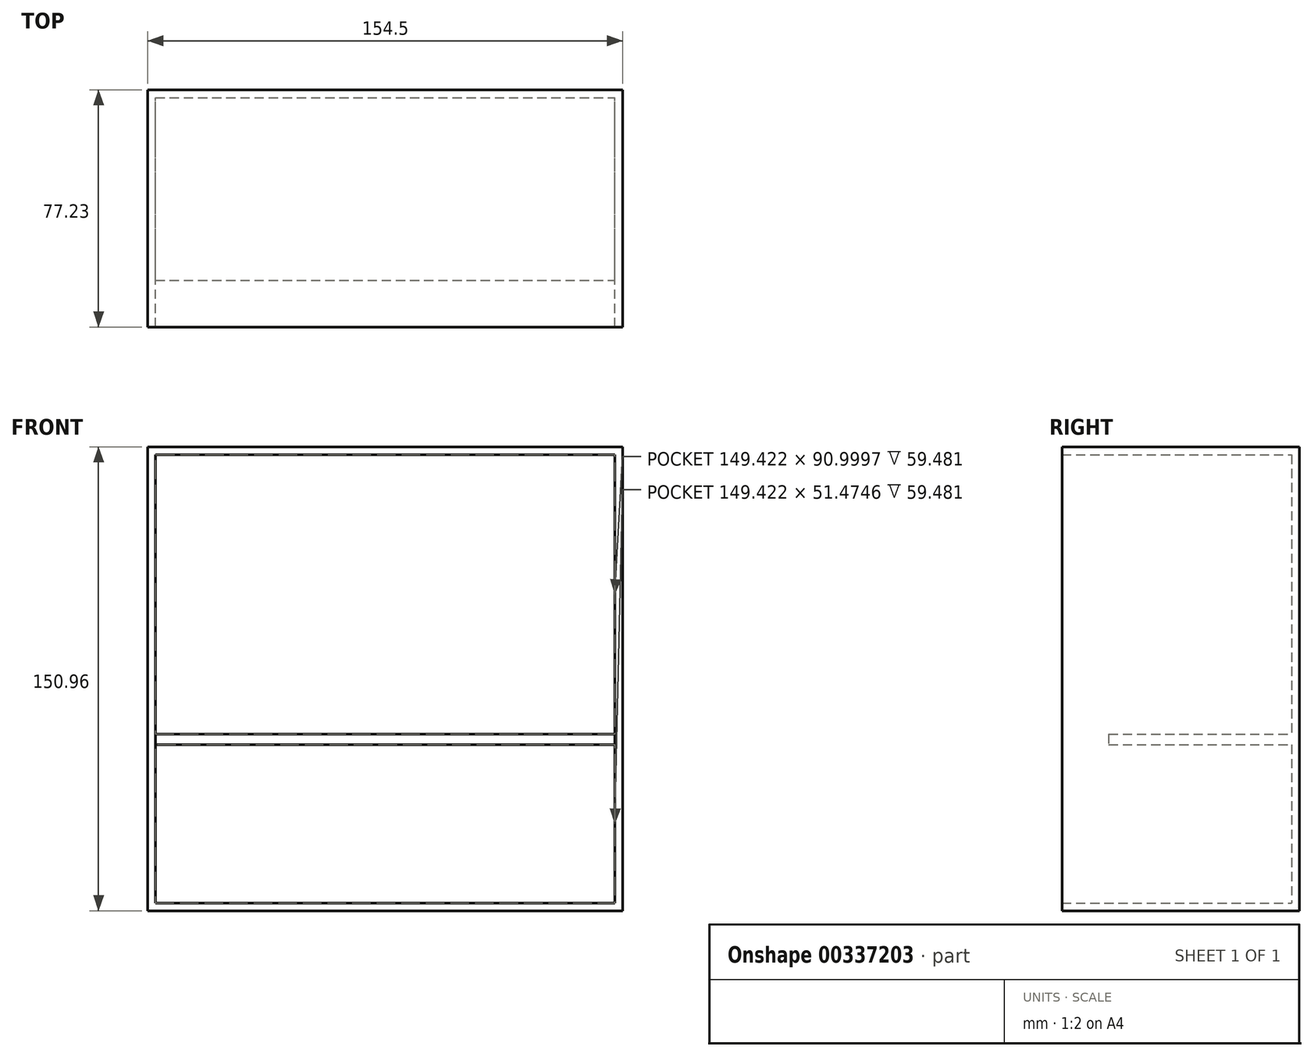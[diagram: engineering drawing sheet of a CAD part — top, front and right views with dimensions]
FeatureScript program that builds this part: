
annotation { "Feature Type Name" : "Feature", "Feature Type Description" : "" }
export const myFeature = defineFeature(function(context is Context, id is Id, definition is map)
    precondition{}
    {
        {
            var Q0;
            Q0=qCreatedBy(makeId("Front.planeOp"),FACE);
            var sketch = newSketch(context, id + "F0", { "sketchPlane" : qUnion([Q0])});
            skLineSegment(sketch, "E0.bottom", {"start": v(77.25, 75.48) * mm, "end": v(-77.25, 75.48) * mm});
            skLineSegment(sketch, "E0.top", {"start": v(77.25, -75.48) * mm, "end": v(-77.25, -75.48) * mm});
            skLineSegment(sketch, "E0.left", {"start": v(77.25, 75.48) * mm, "end": v(77.25, -75.48) * mm});
            skLineSegment(sketch, "E0.right", {"start": v(-77.25, 75.48) * mm, "end": v(-77.25, -75.48) * mm});
            skPoint(sketch, "E0.middle", {"position": v(0, 0) * mm});
            skSolve(sketch);
        }
        {
            var Q0;
            Q0=makeQuery(id+"F0.imprint","IMPRINT",FACE,{"disambiguationData":[TD([[makeQuery(id+"F0.imprint","IMPRINT",EDGE,{"derivedFrom":sQuery(id+"F0.wireOp",EDGE,"E0.bottom")}),1.0]])]});
            var sketch = newSketch(context, id + "F1", { "sketchPlane" : qUnion([Q0])});
            skSolve(sketch);
        }
        {
            var Q0;
            Q0=makeQuery(id+"F1.imprint","IMPRINT",FACE,{"disambiguationData":[TD([[makeQuery(id+"F1.imprint","IMPRINT",EDGE,{"derivedFrom":makeQuery(id+"F0.imprint","IMPRINT",EDGE,{"derivedFrom":sQuery(id+"F0.wireOp",EDGE,"E0.bottom")})}),1.0]])]});
            extrude(context, id + "F2", {"entities" : qUnion([Q0]), "depth" : 77.23 * mm});
        }
        {
            var Q0;
            Q0=makeQuery(id+"F2.opExtrude","CAP_FACE",FACE,{"disambiguationData":[OSD([sQuery(id+"F0.wireOp",EDGE,"E0.bottom"),sQuery(id+"F0.wireOp",EDGE,"E0.top"),sQuery(id+"F0.wireOp",EDGE,"E0.left"),sQuery(id+"F0.wireOp",EDGE,"E0.right")])],"isStart":false});
            shell(context, id + "F3", {"entities" : qUnion([Q0]), "thickness" : 2.54 * mm});
        }
        {
            var Q0;
            Q0=makeQuery(id+"F3.opShell","OFFSET_FACE",FACE,{"disambiguationData":[OSD([sQuery(id+"F0.wireOp",EDGE,"E0.bottom"),sQuery(id+"F0.wireOp",EDGE,"E0.top"),sQuery(id+"F0.wireOp",EDGE,"E0.left"),sQuery(id+"F0.wireOp",EDGE,"E0.right")])]});
            var sketch = newSketch(context, id + "F4", { "sketchPlane" : qUnion([Q0])});
            skLineSegment(sketch, "E1.bottom", {"start": v(-74.71, -21.47) * mm, "end": v(74.71, -21.47) * mm});
            skLineSegment(sketch, "E1.top", {"start": v(-74.71, -18.06) * mm, "end": v(74.71, -18.06) * mm});
            skLineSegment(sketch, "E1.left", {"start": v(-74.71, -21.47) * mm, "end": v(-74.71, -18.06) * mm});
            skLineSegment(sketch, "E1.right", {"start": v(74.71, -21.47) * mm, "end": v(74.71, -18.06) * mm});
            skSolve(sketch);
        }
        {
            var Q0;
            Q0=makeQuery(id+"F4.imprint","IMPRINT",FACE,{"disambiguationData":[TD([[makeQuery(id+"F4.imprint","IMPRINT",EDGE,{"derivedFrom":sQuery(id+"F4.wireOp",EDGE,"E1.bottom")}),1.0]])]});
            extrude(context, id + "F5", {"entities" : qUnion([Q0]), "operationType" : NewBodyOperationType.ADD, "depth" : 59.48 * mm});
        }
    });
